# Revit family: Lira Soap Bottle Holder -  Double
name_source: partatom
category: Generic Models
units: mm (PartAtom-declared; Revit-internal decimal feet)

## family parameters
Always vertical = Yes
Can host rebar = No
Cut with Voids When Loaded = No
Maintain Annotation Orientation = No
OmniClass Number = 23.31.00.00
Part Type = Normal
Room Calculation Point = No
Round Connector Dimension = Use Diameter
Shared = No
Work Plane-Based = No

## types (1)
- LIRA Soap Bottle Holder -  Double
    Catalog web link = https://www.abiinteriors.com.au
    Category = Accessories
    Default Elevation = 0 mm  [stored 0 ft]
    Description = LIRA Soap Bottle Holder - Double
    Keywords = Soap Bottle, Holder
    Manufacturer = ABI Interiors Pty Ltd
    Material = Stainless Steel AISI 304
    Model = 14470
    Part Number = 14470 (BRASS), 14471 (COPPER), 14472 (GUN), 14473 (NICKEL), 14474 (MATTE BLACK), 14475 (WHITE)
    Title = LIRA Soap Bottle Holder - Double
    URL = https://www.abiinteriors.com.au
    Volume = 0 m³

note: [stored X ft] marks values corroborated as IEEE doubles in the binary element streams (Revit-internal decimal feet)

## geometry (parser evidence)
native form markers: Sweep x3
no freeform markers — native parametric forms only
